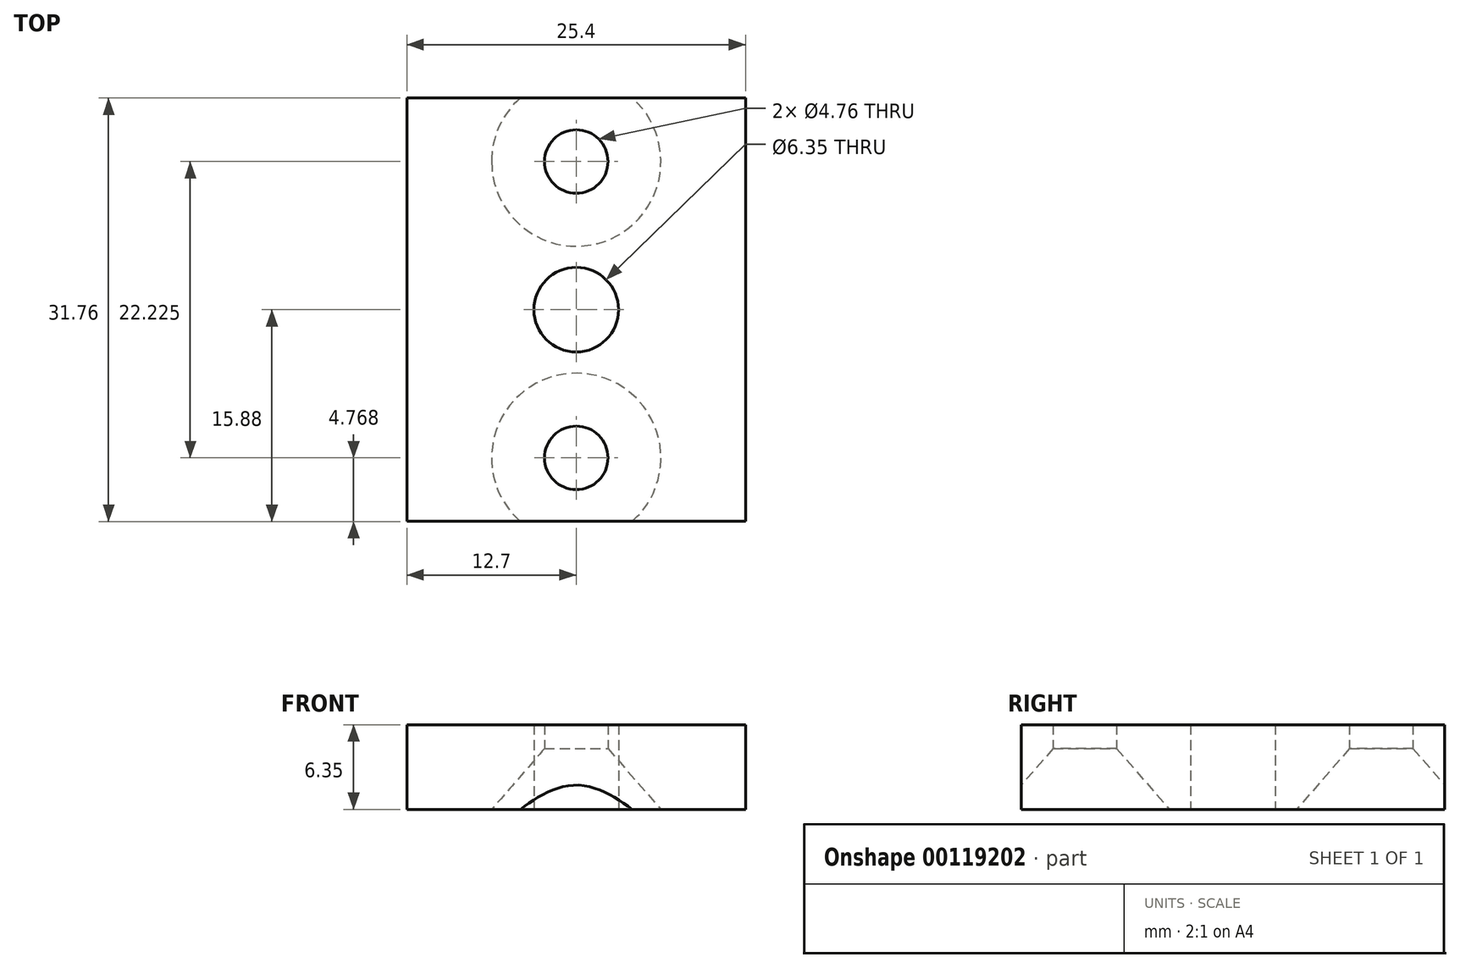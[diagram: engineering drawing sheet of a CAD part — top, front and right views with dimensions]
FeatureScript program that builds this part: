
annotation { "Feature Type Name" : "Feature", "Feature Type Description" : "" }
export const myFeature = defineFeature(function(context is Context, id is Id, definition is map)
    precondition{}
    {
        {
            var Q0;
            Q0=qCreatedBy(makeId("Top.planeOp"),FACE);
            var sketch = newSketch(context, id + "F0", { "sketchPlane" : qUnion([Q0])});
            skLineSegment(sketch, "E0.bottom", {"start": v(-12.7, -15.88) * mm, "end": v(12.7, -15.88) * mm});
            skLineSegment(sketch, "E0.top", {"start": v(-12.7, 15.88) * mm, "end": v(12.7, 15.88) * mm});
            skLineSegment(sketch, "E0.left", {"start": v(-12.7, -15.88) * mm, "end": v(-12.7, 15.88) * mm});
            skLineSegment(sketch, "E0.right", {"start": v(12.7, -15.88) * mm, "end": v(12.7, 15.88) * mm});
            skPoint(sketch, "E0.middle", {"position": v(0, 0) * mm});
            skCircle(sketch, "E1", {"center": v(0, 0) * mm, "radius": 3.18 * mm});
            skCircle(sketch, "E2", {"center": v(0, 11.11) * mm, "radius": 2.38 * mm});
            skCircle(sketch, "E3", {"center": v(0, -11.11) * mm, "radius": 2.38 * mm});
            skLineSegment(sketch, "E4", {"start": v(0, 15.88) * mm, "end": v(0, 11.11) * mm});
            skLineSegment(sketch, "E5", {"start": v(0, -11.11) * mm, "end": v(0, 0) * mm});
            skLineSegment(sketch, "E6", {"start": v(0, 11.11) * mm, "end": v(0, 0) * mm});
            skLineSegment(sketch, "E7", {"start": v(0, -11.11) * mm, "end": v(0, -15.88) * mm});
            skSolve(sketch);
        }
        {
            var Q0;
            {var subQ5=sQuery(id+"F0.wireOp",EDGE,"E0.left");Q0=makeQuery(id+"F0.imprint","IMPRINT",FACE,{"disambiguationData":[TD([[makeQuery(id+"F0.imprint","IMPRINT",EDGE,{"derivedFrom":subQ5}),-1.0]])]});}
            var Q1;
            {var subQ7=sQuery(id+"F0.wireOp",EDGE,"E0.right");Q1=makeQuery(id+"F0.imprint","IMPRINT",FACE,{"disambiguationData":[TD([[makeQuery(id+"F0.imprint","IMPRINT",EDGE,{"derivedFrom":subQ7}),1.0]])]});}
            extrude(context, id + "F1", {"entities" : qUnion([Q0, Q1]), "depth" : 6.35 * mm});
        }
        {
            var Q0;
            Q0=sQuery(id+"F0.wireOp",VERTEX,"E6.start");
            var Q1;
            Q1=sQuery(id+"F0.wireOp",VERTEX,"E5.start");
            var Q2;
            Q2=makeQuery(id+"F1.opExtrude","SWEPT_BODY",BODY,{"disambiguationData":[OSD([sQuery(id+"F0.wireOp",EDGE,"E0.bottom"),sQuery(id+"F0.wireOp",EDGE,"E0.top"),sQuery(id+"F0.wireOp",EDGE,"E0.left"),sQuery(id+"F0.wireOp",EDGE,"E0.right"),sQuery(id+"F0.wireOp",EDGE,"E1"),sQuery(id+"F0.wireOp",EDGE,"E2"),sQuery(id+"F0.wireOp",EDGE,"E3")])]});
            hole(context, id + "F2", {"style" : HoleStyle.C_SINK, "endStyle" : HoleEndStyle.THROUGH, "oppositeDirection" : true, "holeDiameter" : 4.76 * mm, "cSinkDiameter" : 12.7 * mm, "cSinkAngle" : 82 * degree, "locations" : qUnion([Q0, Q1]), "scope" : qUnion([Q2]), "isTappedThrough" : true});
        }
    });
